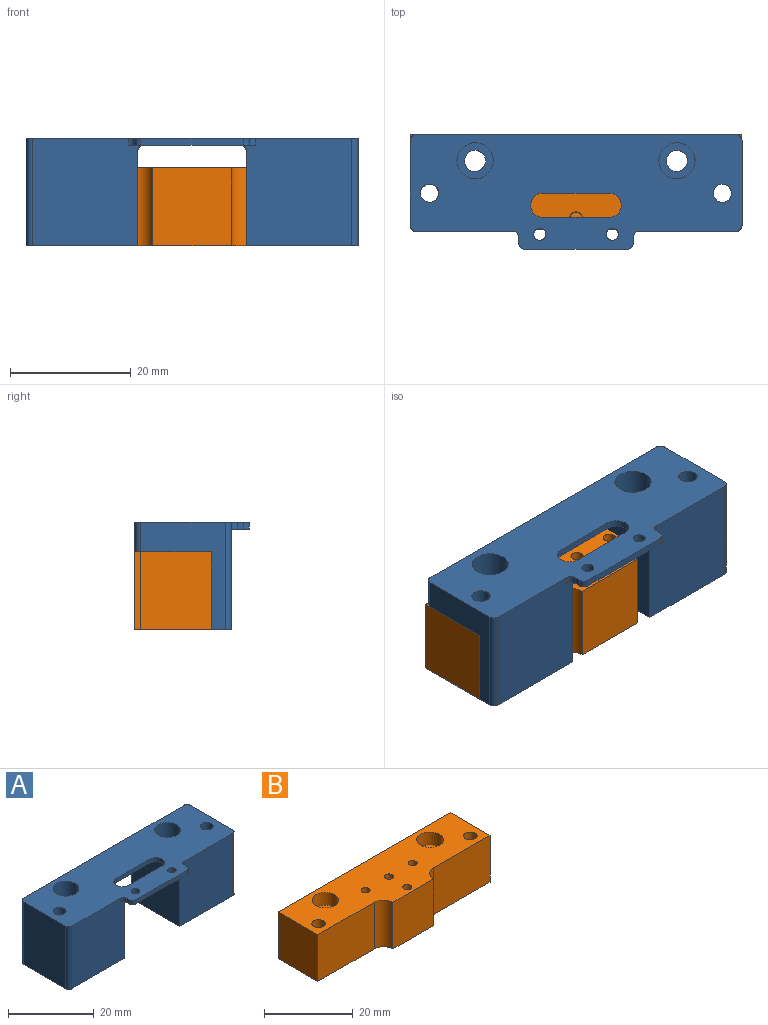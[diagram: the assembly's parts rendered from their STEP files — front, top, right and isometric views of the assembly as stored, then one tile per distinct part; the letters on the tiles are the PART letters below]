
ASSEMBLY  parts=2 mates=1
PART A: 38 faces, bbox 55x19x17.8 mm
  f0: cylinder r=1.75mm len=10.81mm, axis (0,0,1), area 118.9mm2, adj f8,f26
  f1: cylinder r=1.75mm len=10.81mm, axis (0,0,1), area 118.9mm2, adj f4,f24
  f2: plane 55x19mm, normal (0,0,1), area 802.4mm2, adj f5,f6,f7,f11,f12,f13,f14,f15
  f3: plane 21x19mm, normal (0,0,-1), area 250.2mm2, adj f5,f6,f7,f11,f13,f14,f18,f19
  f4: plane 18.5x16mm, normal (0,0,-1), area 278.8mm2, adj f1,f10,f11,f14,f15,f17,f36,f37
  f5: plane 1.15x1mm, normal (1,0,0), area 1.1mm2, adj f2,f3,f34,f35
  f6: plane 17x1.15mm, normal (0,-1,0), area 19.5mm2, adj f2,f3,f33,f34
  f7: plane 1.15x1mm, normal (-1,0,0), area 1.1mm2, adj f2,f3,f32,f33
  f8: plane 18.5x16mm, normal (0,0,-1), area 278.8mm2, adj f0,f9,f11,f12,f13,f16,f30,f31
  f9: plane 16x15.66mm, normal (1,0,0), area 250.6mm2, adj f8,f11,f13,f29
  f10: plane 16x15.66mm, normal (-1,0,0), area 250.6mm2, adj f4,f11,f14,f28
  f11: plane 53x17.81mm, normal (0,1,0), area 644.5mm2, adj f2,f3,f4,f8,f9,f10,f28,f29
  f12: plane 17.81x14mm, normal (-1,0,0), area 249.3mm2, adj f2,f8,f30,f31
  f13: plane 18.5x17.81mm, normal (0,-1,0), area 310.2mm2, adj f2,f3,f8,f9,f29,f31,f32
  f14: plane 18.5x17.81mm, normal (0,-1,0), area 310.2mm2, adj f2,f3,f4,f10,f28,f35,f36
  f15: plane 17.81x14mm, normal (1,0,0), area 249.3mm2, adj f2,f4,f36,f37
  f16: cylinder r=1.51mm len=17.81mm, axis (0,0,1), area 169mm2, adj f2,f8
  f17: cylinder r=1.51mm len=17.81mm, axis (0,0,1), area 169mm2, adj f2,f4
  f18: cylinder r=1mm len=2mm, axis (0,0,1), area 7.2mm2, adj f2,f3
  f19: cylinder r=1mm len=2mm, axis (0,0,1), area 7.2mm2, adj f2,f3
  f20: plane 11x1.15mm, normal (0,-1,0), area 12.6mm2, adj f2,f3,f21,f23
  f21: cylinder r=2mm len=4mm, axis (0,0,1), area 7.2mm2, adj f2,f3,f20,f22
  f22: plane 11x1.15mm, normal (0,1,0), area 12.6mm2, adj f2,f3,f21,f23
  f23: cylinder r=2mm len=4mm, axis (0,0,1), area 7.2mm2, adj f2,f3,f20,f22
  f24: plane 6x6mm, normal (0,0,1), area 18.7mm2, adj f1,f25
  f25: cylinder r=3mm len=7mm, axis (0,0,1), area 131.9mm2, adj f2,f24
  f26: plane 6x6mm, normal (0,0,1), area 18.7mm2, adj f0,f27
  f27: cylinder r=3mm len=7mm, axis (0,0,1), area 131.9mm2, adj f2,f26
  f28: cylinder r=1mm len=16mm, axis (0,-1,0), area 25.1mm2, adj f3,f10,f11,f14
  f29: cylinder r=1mm len=16mm, axis (0,1,0), area 25.1mm2, adj f3,f9,f11,f13
  f30: cylinder r=1mm len=17.81mm, axis (0,0,-1), area 28mm2, adj f2,f8,f11,f12
  f31: cylinder r=1mm len=17.81mm, axis (0,0,-1), area 28mm2, adj f2,f8,f12,f13
  f32: cylinder r=1mm len=1.15mm, axis (0,0,1), area 1.8mm2, adj f2,f3,f7,f13
  f33: cylinder r=1mm len=1.15mm, axis (0,0,-1), area 1.8mm2, adj f2,f3,f6,f7
  f34: cylinder r=1mm len=1.15mm, axis (0,0,-1), area 1.8mm2, adj f2,f3,f5,f6
  f35: cylinder r=1mm len=1.15mm, axis (0,0,1), area 1.8mm2, adj f2,f3,f5,f14
  f36: cylinder r=1mm len=17.81mm, axis (0,0,-1), area 28mm2, adj f2,f4,f14,f15
  f37: cylinder r=1mm len=17.81mm, axis (0,0,-1), area 28mm2, adj f2,f4,f11,f15
PART B: 24 faces, bbox 55x15.7x12.9 mm
  f0: cylinder r=1.75mm len=9.41mm, axis (0,0,1), area 103.5mm2, adj f9,f16
  f1: cylinder r=1.75mm len=9.41mm, axis (0,0,1), area 103.5mm2, adj f9,f14
  f2: plane 55x12.91mm, normal (0,1,0), area 710mm2, adj f3,f7,f8,f9
  f3: plane 12.91x12.7mm, normal (-1,0,0), area 164mm2, adj f2,f4,f8,f9
  f4: plane 18x12.91mm, normal (0,-1,0), area 232.4mm2, adj f3,f8,f9,f22
  f5: plane 13x12.91mm, normal (0,-1,0), area 167.8mm2, adj f8,f9,f22,f23
  f6: plane 18x12.91mm, normal (0,-1,0), area 232.4mm2, adj f7,f8,f9,f23
  f7: plane 12.91x12.7mm, normal (1,0,0), area 164mm2, adj f2,f6,f8,f9
  f8: plane 55x15.7mm, normal (0,0,1), area 657.6mm2, adj f2,f3,f4,f5,f6,f7,f10,f11
  f9: plane 55x15.7mm, normal (0,0,-1), area 701.5mm2, adj f0,f1,f2,f3,f4,f5,f6,f7
  f10: cylinder r=1mm len=12.91mm, axis (0,0,1), area 81.1mm2, adj f8,f9
  f11: cylinder r=1.51mm len=12.91mm, axis (0,0,1), area 122.5mm2, adj f8,f9
  f12: cylinder r=1.51mm len=12.91mm, axis (0,0,1), area 122.5mm2, adj f8,f9
  f13: cylinder r=1mm len=12.91mm, axis (0,0,1), area 81.1mm2, adj f8,f9
  f14: plane 6x6mm, normal (0,0,1), area 18.7mm2, adj f1,f15
  f15: cylinder r=3mm len=6mm, axis (0,0,1), area 66mm2, adj f8,f14
  f16: plane 6x6mm, normal (0,0,1), area 18.7mm2, adj f0,f17
  f17: cylinder r=3mm len=6mm, axis (0,0,1), area 66mm2, adj f8,f16
  f18: cylinder r=1.03mm len=6mm, axis (0,0,1), area 38.6mm2, adj f8,f19
  f19: plane 2.05x2.05mm, normal (0,0,1), area 3.3mm2, adj f18
  f20: cylinder r=1.03mm len=6mm, axis (0,0,1), area 38.6mm2, adj f8,f21
  f21: plane 2.05x2.05mm, normal (0,0,1), area 3.3mm2, adj f20
  f22: cylinder r=3mm len=12.91mm, axis (0,0,1), area 60.8mm2, adj f4,f5,f8,f9
  f23: cylinder r=3mm len=12.91mm, axis (0,0,1), area 60.8mm2, adj f5,f6,f8,f9
PLACE A t=(-26.46,56.54,30.51)mm
PLACE B t=(-56.22,95.81,30.51)mm
MATE slider B.f12 <-> A.f17  axis (0,0,1) through (-4.47,86.11,43.42)mm
